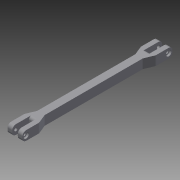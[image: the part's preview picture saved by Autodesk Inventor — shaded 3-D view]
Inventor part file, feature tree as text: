
AUTODESK INVENTOR PART (.ipt)
format: ipt  version: 2015 (Build 190159000, 159)  size: 166,912 bytes
history: native  units: mm
features: sketch x4, fillet x4, extrude x2, plane x2, mirror x2, loft x1, hole x1, other x1
ambient origin geometry x8: Origin, YZ Plane, XZ Plane, XY Plane, X Axis, Y Axis, Z Axis, Center Point
bodies: Solid1 (feature_tree)
feature tree (17):
  extrude  "Extrusion1"  Depth=10.0mm
  sketch  "Sketch2"  dims[d2=126.0mm d3=0.0mm d4=5.0mm]
  sketch  "Sketch3"  dims[d5=5.0mm d6=3.05mm d7=3.05mm d8=10.0mm]
  extrude  "Extrusion3"  Depth=5.0mm
  loft  "Loft2"
  plane  "Work Plane2"
  fillet  "Fillet4"  Radius=3.05mm
  fillet  "Fillet5"  Radius=10.0mm
  hole  "Hole1"  [1 undecoded]
  mirror  "Mirror2"
  plane  "Work Plane3"
  mirror  "Mirror3"
  fillet  "Fillet6"  [1 undecoded]
  fillet  "Fillet7"  Radius=4.0mm
  sketch  "Sketch1"  dims[d0=8.0mm d1=10.0mm]
  other  "Edges1"
  sketch  "Sketch5"  dims[d18=18.0mm d19=0.0mm d20=0.0mm d21=90.0deg d22=0.0mm d23=90.0deg d24=4.0mm d25=4.0mm d26=3.3mm d27=6.0mm d28=6.0mm d29=2.0mm d30=90.0deg d31=8.0mm d32=20.594885mm d42=3.0mm d43=3.0mm]
note: 2 required parameter values undecoded (feature->parameter linkage not recoverable at this tier; creation-order binding heuristic only, values carry confidence <= 0.55)
